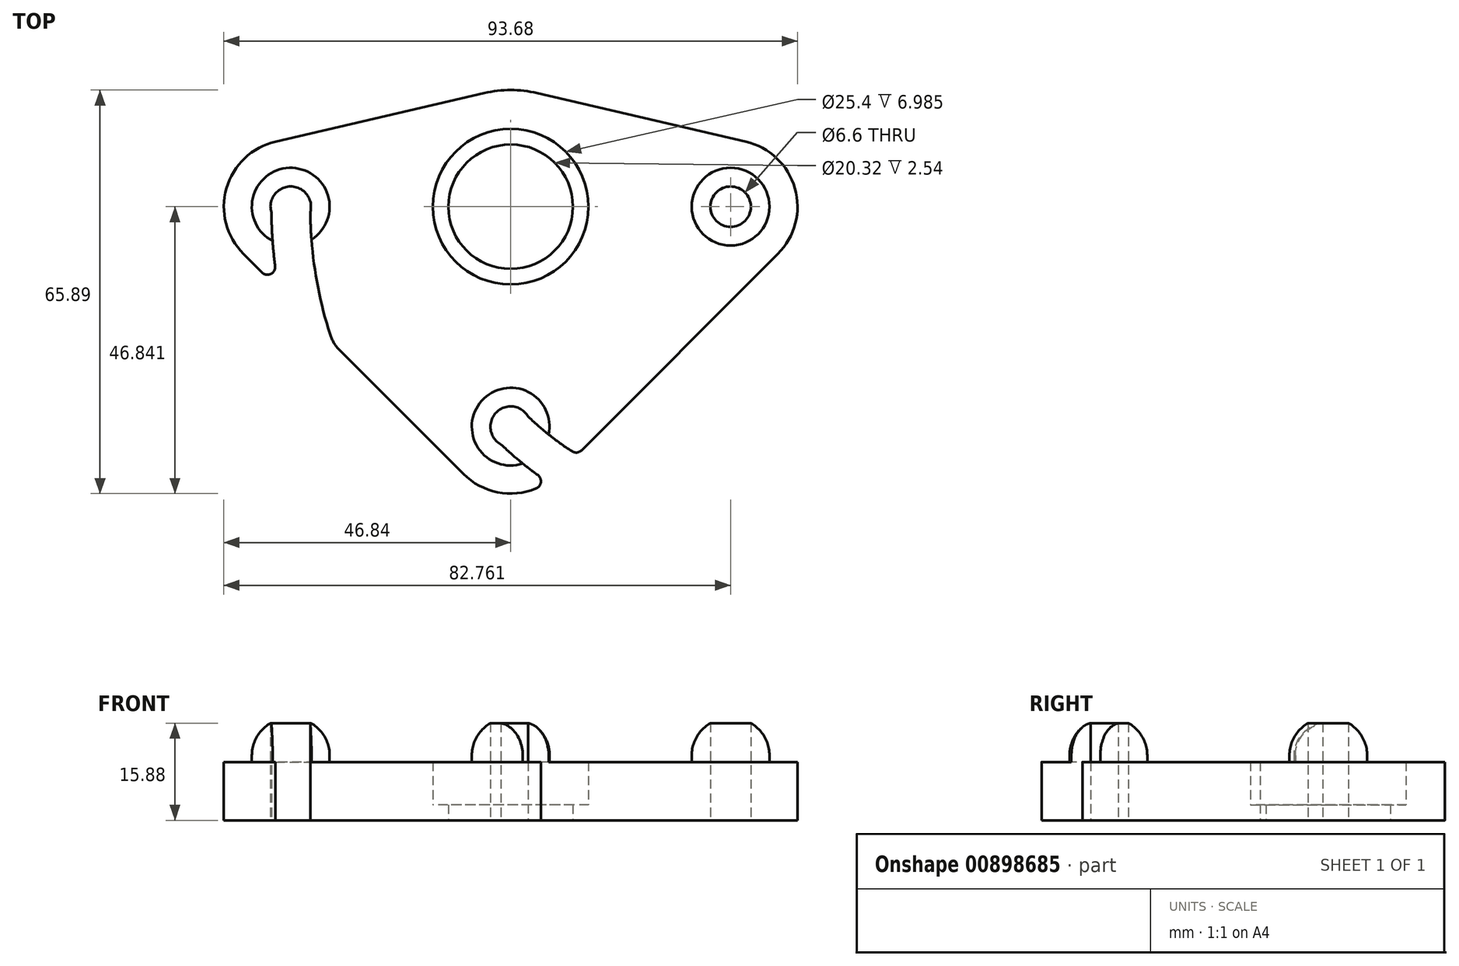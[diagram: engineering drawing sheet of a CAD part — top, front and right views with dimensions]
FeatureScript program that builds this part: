
annotation { "Feature Type Name" : "Feature", "Feature Type Description" : "" }
export const myFeature = defineFeature(function(context is Context, id is Id, definition is map)
    precondition{}
    {
        {
            var Q0;
            Q0=qCreatedBy(makeId("Top.planeOp"),FACE);
            var sketch = newSketch(context, id + "F0", { "sketchPlane" : qUnion([Q0])});
            skCircle(sketch, "E0", {"center": v(0, 35.92) * mm, "radius": 12.7 * mm});
            skArc(sketch, "E1.0", {"start": v(4.31, 54.48) * mm, "mid": v(0, 54.97) * mm, "end": v(-4.31, 54.48) * mm});
            skLineSegment(sketch, "E2", {"start": v(-38.4, 46.56) * mm, "end": v(-4.31, 54.48) * mm});
            skLineSegment(sketch, "E3", {"start": v(4.31, 54.48) * mm, "end": v(38.4, 46.56) * mm});
            skCircle(sketch, "E4.0", {"center": v(0, 35.92) * mm, "radius": 10.16 * mm});
            skLineSegment(sketch, "E5", {"start": v(0, 35.92) * mm, "end": v(0, 48.62) * mm, "construction": true});
            skLineSegment(sketch, "E6", {"start": v(-35.92, 35.92) * mm, "end": v(35.92, 35.92) * mm, "construction": true});
            skCircle(sketch, "E7", {"center": v(35.92, 35.92) * mm, "radius": 3.3 * mm});
            skArc(sketch, "E8", {"start": v(-32.74, 35.03) * mm, "mid": v(-35.94, 39.22) * mm, "end": v(-39.1, 35) * mm});
            skArc(sketch, "E9.0", {"start": v(-38.4, 46.56) * mm, "mid": v(-46.42, 38.92) * mm, "end": v(-43.64, 28.2) * mm});
            skArc(sketch, "E10.0", {"start": v(-7.72, -7.72) * mm, "mid": v(-2.15, -10.7) * mm, "end": v(4.15, -10.1) * mm});
            skArc(sketch, "E11.0", {"start": v(43.64, 28.2) * mm, "mid": v(46.42, 38.92) * mm, "end": v(38.4, 46.56) * mm});
            skLineSegment(sketch, "E12", {"start": v(-43.64, 28.2) * mm, "end": v(-40.63, 25.18) * mm});
            skLineSegment(sketch, "E13", {"start": v(11.58, -3.86) * mm, "end": v(43.64, 28.2) * mm});
            skCircle(sketch, "E14", {"center": v(0, 0) * mm, "radius": 3.18 * mm, "construction": true});
            skCircle(sketch, "E15", {"center": v(-35.92, 35.92) * mm, "radius": 3.18 * mm, "construction": true});
            skArc(sketch, "E16", {"start": v(-32.74, 36.8) * mm, "mid": v(-32, 25.8) * mm, "end": v(-29.5, 15.05) * mm});
            skArc(sketch, "E17", {"start": v(-39.1, 35.92) * mm, "mid": v(-38.94, 31.07) * mm, "end": v(-38.47, 26.24) * mm});
            skLineSegment(sketch, "E18.trimOffspring", {"start": v(-27.94, 12.5) * mm, "end": v(-7.72, -7.72) * mm});
            skArc(sketch, "E19", {"start": v(2.87, 1.63) * mm, "mid": v(-2.36, 2.31) * mm, "end": v(-1.58, -2.9) * mm});
            skArc(sketch, "E20", {"start": v(-2.25, -2.25) * mm, "mid": v(0.97, -5.2) * mm, "end": v(4.4, -7.9) * mm});
            skArc(sketch, "E21.trimOffspring", {"start": v(2.25, 2.25) * mm, "mid": v(5.96, -1.1) * mm, "end": v(10, -4.03) * mm});
            skPoint(sketch, "E22.visualSharp", {"position": v(-29, 13.56) * mm});
            skArc(sketch, "E22.filletArc", {"start": v(-29.5, 15.05) * mm, "mid": v(-28.87, 13.68) * mm, "end": v(-27.94, 12.5) * mm});
            skPoint(sketch, "E23.visualSharp", {"position": v(-37.87, 22.43) * mm});
            skArc(sketch, "E23.filletArc", {"start": v(-40.63, 25.18) * mm, "mid": v(-39.17, 24.94) * mm, "end": v(-38.47, 26.24) * mm});
            skPoint(sketch, "E24.visualSharp", {"position": v(6.1, -9.06) * mm});
            skArc(sketch, "E24.filletArc", {"start": v(4.15, -10.1) * mm, "mid": v(4.93, -9.08) * mm, "end": v(4.4, -7.9) * mm});
            skPoint(sketch, "E25.visualSharp", {"position": v(10.87, -4.58) * mm});
            skArc(sketch, "E25.filletArc", {"start": v(10, -4.03) * mm, "mid": v(10.82, -4.23) * mm, "end": v(11.58, -3.86) * mm});
            skSolve(sketch);
        }
        {
            var Q0;
            Q0=makeQuery(id+"F0.imprint","IMPRINT",FACE,{"disambiguationData":[TD([[makeQuery(id+"F0.imprint","IMPRINT",EDGE,{"derivedFrom":sQuery(id+"F0.wireOp",EDGE,"E0")}),-1.0]])]});
            extrude(context, id + "F1", {"entities" : qUnion([Q0]), "depth" : 9.52 * mm, "offsetDistance" : 25.4 * mm});
        }
        {
            var Q0;
            Q0=makeQuery(id+"F0.imprint","IMPRINT",FACE,{"disambiguationData":[TD([[makeQuery(id+"F0.imprint","IMPRINT",EDGE,{"derivedFrom":sQuery(id+"F0.wireOp",EDGE,"E0")}),1.0]])]});
            var Q1;
            Q1=makeQuery(id+"F1.opExtrude","CAP_FACE",FACE,{"disambiguationData":[OSD([sQuery(id+"F0.wireOp",EDGE,"EjYE8rPL-0voM-13ep-dpKR-Yhmu4oC0fMjX"),sQuery(id+"F0.wireOp",EDGE,"BDsdlpYl-4XZS-kb72-SQzJ-jy24um5DGsSm"),sQuery(id+"F0.wireOp",EDGE,"zDj9rnkT-zBYQ-YRrf-FuGE-prHvdQQL9E0l"),sQuery(id+"F0.wireOp",EDGE,"E0"),sQuery(id+"F0.wireOp",EDGE,"be656b23-60e4-4951-9072-4bb9fd2c1fe0.0"),sQuery(id+"F0.wireOp",EDGE,"E1.0"),sQuery(id+"F0.wireOp",EDGE,"4a9f2f50-e787-4006-96f4-ab8e54a99077.0"),sQuery(id+"F0.wireOp",EDGE,"02fbeba7-076e-4ed0-9f02-67362b93dccf.0"),sQuery(id+"F0.wireOp",EDGE,"E2"),sQuery(id+"F0.wireOp",EDGE,"E3"),sQuery(id+"F0.wireOp",EDGE,"O9yRHGw0-B6N5-WUBC-CqYZ-9fVMz9zkHXct"),sQuery(id+"F0.wireOp",EDGE,"bXI39tXD-kIKO-QA8d-uo1d-AjNWw4kzWSzn"),sQuery(id+"F0.wireOp",EDGE,"yvXXFvSa-JQHm-aZvy-wO3q-0ffgoC5Wr51Q"),sQuery(id+"F0.wireOp",EDGE,"keBa6mA6-Ns36-as4S-D7yK-ubB9MYcM4YDE"),sQuery(id+"F0.wireOp",EDGE,"8eHimBAp-EooJ-JMgW-8GNK-FZK91k5yhUmU"),sQuery(id+"F0.wireOp",EDGE,"36RZBXD3-6qK0-qw5N-QxHJ-8RBiURi620yN"),sQuery(id+"F0.wireOp",EDGE,"1b80de2d-6fcf-4166-8bd7-bc7520118ab3.trimOffspring"),sQuery(id+"F0.wireOp",EDGE,"c2b8b45b-57a7-46a8-b7ff-993cbbd2993e.trimOffspring"),sQuery(id+"F0.wireOp",EDGE,"9e57da74-859c-4f91-937b-fdcaf8afdda5.filletArc"),sQuery(id+"F0.wireOp",EDGE,"30e6a12d-ff62-4460-809b-2951cf116d4f.filletArc"),sQuery(id+"F0.wireOp",EDGE,"3d167f00-72a4-4ff5-8a6d-0d591a0e7773.filletArc"),sQuery(id+"F0.wireOp",EDGE,"oY1VHBi5-08zZ-AYfj-pQcV-54PoHM0Vimur"),sQuery(id+"F0.wireOp",EDGE,"o9Ub0ZbI-FWSb-Ar0A-mzkB-0TMMgAmCBTNA"),sQuery(id+"F0.wireOp",EDGE,"02ed80ea-b338-46f1-988c-5186e078d909.trimOffspring"),sQuery(id+"F0.wireOp",EDGE,"5048e359-dd0b-4d89-8e95-103b38747b91.filletArc"),sQuery(id+"F0.wireOp",EDGE,"F9NU9Cbi-ggXa-7yM7-VtZo-IDbmedrVVywU"),sQuery(id+"F0.wireOp",EDGE,"RxFEJMYw-qQQS-0Qhc-ig3X-IfwXJgG6lVj4"),sQuery(id+"F0.wireOp",EDGE,"25558c64-657d-4b99-b26e-c29775e7ec7f.filletArc"),sQuery(id+"F0.wireOp",EDGE,"0ec6c237-3fc5-43e5-bd65-df81ba4ec1d8.filletArc"),sQuery(id+"F0.wireOp",EDGE,"df5fecd0-7309-4179-a44a-8c306f083116.filletArc"),sQuery(id+"F0.wireOp",EDGE,"e0a676b0-1f90-490a-bc8b-b1ab685ed8d2.filletArc")])],"isStart":false});
            extrude(context, id + "F2", {"entities" : qUnion([Q0]), "operationType" : NewBodyOperationType.ADD, "depth" : 2.54 * mm, "endBoundEntityFace" : qUnion([Q1]), "offsetDistance" : 6.35 * mm});
        }
        {
            var Q0;
            Q0=makeQuery(id+"F1.opExtrude","CAP_FACE",FACE,{"disambiguationData":[OSD([sQuery(id+"F0.wireOp",EDGE,"EjYE8rPL-0voM-13ep-dpKR-Yhmu4oC0fMjX"),sQuery(id+"F0.wireOp",EDGE,"BDsdlpYl-4XZS-kb72-SQzJ-jy24um5DGsSm"),sQuery(id+"F0.wireOp",EDGE,"zDj9rnkT-zBYQ-YRrf-FuGE-prHvdQQL9E0l"),sQuery(id+"F0.wireOp",EDGE,"E0"),sQuery(id+"F0.wireOp",EDGE,"be656b23-60e4-4951-9072-4bb9fd2c1fe0.0"),sQuery(id+"F0.wireOp",EDGE,"E1.0"),sQuery(id+"F0.wireOp",EDGE,"4a9f2f50-e787-4006-96f4-ab8e54a99077.0"),sQuery(id+"F0.wireOp",EDGE,"02fbeba7-076e-4ed0-9f02-67362b93dccf.0"),sQuery(id+"F0.wireOp",EDGE,"E2"),sQuery(id+"F0.wireOp",EDGE,"E3"),sQuery(id+"F0.wireOp",EDGE,"O9yRHGw0-B6N5-WUBC-CqYZ-9fVMz9zkHXct"),sQuery(id+"F0.wireOp",EDGE,"bXI39tXD-kIKO-QA8d-uo1d-AjNWw4kzWSzn"),sQuery(id+"F0.wireOp",EDGE,"yvXXFvSa-JQHm-aZvy-wO3q-0ffgoC5Wr51Q"),sQuery(id+"F0.wireOp",EDGE,"keBa6mA6-Ns36-as4S-D7yK-ubB9MYcM4YDE"),sQuery(id+"F0.wireOp",EDGE,"8eHimBAp-EooJ-JMgW-8GNK-FZK91k5yhUmU"),sQuery(id+"F0.wireOp",EDGE,"36RZBXD3-6qK0-qw5N-QxHJ-8RBiURi620yN"),sQuery(id+"F0.wireOp",EDGE,"1b80de2d-6fcf-4166-8bd7-bc7520118ab3.trimOffspring"),sQuery(id+"F0.wireOp",EDGE,"c2b8b45b-57a7-46a8-b7ff-993cbbd2993e.trimOffspring"),sQuery(id+"F0.wireOp",EDGE,"9e57da74-859c-4f91-937b-fdcaf8afdda5.filletArc"),sQuery(id+"F0.wireOp",EDGE,"30e6a12d-ff62-4460-809b-2951cf116d4f.filletArc"),sQuery(id+"F0.wireOp",EDGE,"3d167f00-72a4-4ff5-8a6d-0d591a0e7773.filletArc"),sQuery(id+"F0.wireOp",EDGE,"oY1VHBi5-08zZ-AYfj-pQcV-54PoHM0Vimur"),sQuery(id+"F0.wireOp",EDGE,"o9Ub0ZbI-FWSb-Ar0A-mzkB-0TMMgAmCBTNA"),sQuery(id+"F0.wireOp",EDGE,"02ed80ea-b338-46f1-988c-5186e078d909.trimOffspring"),sQuery(id+"F0.wireOp",EDGE,"3LgmcLzA-5pnU-fFz7-q1u9-bpeBtAsCO3An"),sQuery(id+"F0.wireOp",EDGE,"4eo9xTR6-c1Fu-en91-zOid-S4E7wj55DmDX"),sQuery(id+"F0.wireOp",EDGE,"5048e359-dd0b-4d89-8e95-103b38747b91.filletArc"),sQuery(id+"F0.wireOp",EDGE,"0de4be46-af92-408f-a28e-b5eb566cc358.filletArc"),sQuery(id+"F0.wireOp",EDGE,"cd97e584-8722-4711-bad1-4d169eb79cda.filletArc"),sQuery(id+"F0.wireOp",EDGE,"a80f9f6f-3806-41d0-9fd0-596e0330244b.filletArc"),sQuery(id+"F0.wireOp",EDGE,"743a1c7c-530f-41f0-bede-06812bb20fe3.filletArc")])],"isStart":false});
            var sketch = newSketch(context, id + "F3", { "sketchPlane" : qUnion([Q0])});
            skCircle(sketch, "E26", {"center": v(-35.92, 35.92) * mm, "radius": 6.35 * mm});
            skCircle(sketch, "E27", {"center": v(35.92, 35.92) * mm, "radius": 6.35 * mm});
            skCircle(sketch, "E28", {"center": v(0, 0) * mm, "radius": 6.35 * mm});
            skSolve(sketch);
        }
        {
            var Q0;
            {var subQ5=makeQuery(id+"F1.opExtrude","CAP_EDGE",EDGE,{"disambiguationData":[OSD([sQuery(id+"F0.wireOp",EDGE,"E8")])],"isStart":false});Q0=makeQuery(id+"F3.imprint","IMPRINT",FACE,{"disambiguationData":[TD([[makeQuery(id+"F3.imprint","IMPRINT",EDGE,{"derivedFrom":subQ5}),-1.0]])]});}
            var Q1;
            {var subQ5=makeQuery(id+"F1.opExtrude","CAP_EDGE",EDGE,{"disambiguationData":[OSD([sQuery(id+"F0.wireOp",EDGE,"E19")])],"isStart":false});Q1=makeQuery(id+"F3.imprint","IMPRINT",FACE,{"disambiguationData":[TD([[makeQuery(id+"F3.imprint","IMPRINT",EDGE,{"derivedFrom":subQ5}),-1.0]])]});}
            var Q2;
            Q2=makeQuery(id+"F3.imprint","IMPRINT",FACE,{"disambiguationData":[TD([[makeQuery(id+"F3.imprint","IMPRINT",EDGE,{"derivedFrom":sQuery(id+"F3.wireOp",EDGE,"E27")}),1.0]])]});
            extrude(context, id + "F4", {"entities" : qUnion([Q0, Q1, Q2]), "operationType" : NewBodyOperationType.ADD, "depth" : 6.35 * mm, "offsetDistance" : 25.4 * mm});
        }
        {
            var Q0;
            Q0=makeQuery(id+"F4.opExtrude","CAP_EDGE",EDGE,{"disambiguationData":[OSD([sQuery(id+"F3.wireOp",EDGE,"E26")])],"isStart":false});
            var Q1;
            Q1=makeQuery(id+"F4.opExtrude","CAP_EDGE",EDGE,{"disambiguationData":[OSD([sQuery(id+"F3.wireOp",EDGE,"E28")])],"isStart":false});
            var Q2;
            Q2=makeQuery(id+"F4.opExtrude","CAP_EDGE",EDGE,{"disambiguationData":[OSD([sQuery(id+"F3.wireOp",EDGE,"E27")])],"isStart":false});
            fillet(context, id + "F5", {"entities" : qUnion([Q0, Q1, Q2]), "radius" : 6.1 * mm, "tangentPropagation" : true, "allowEdgeOverflow" : false});
        }
    });
